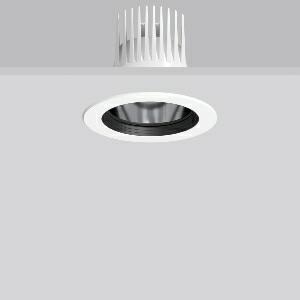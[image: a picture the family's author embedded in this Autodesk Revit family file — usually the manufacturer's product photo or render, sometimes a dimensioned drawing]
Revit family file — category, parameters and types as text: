
# Revit family: heledon_maxi_e_901763_002_1_8824
name_source: partatom
category: Lighting Fixtures
units: mm (PartAtom-declared; Revit-internal decimal feet)

## family parameters
Cut with Voids When Loaded = No
Host = Face
Light Source = No
Part Type = Normal
Room Calculation Point = No
Round Connector Dimension = Use Diameter
Shared = No

## types (1)
- HELEDON maxi E (1 x LED Modul 940, 4400 lm, 4000)
    Apparent Load = 35 VA
    Approval mark = CE
    CIE Flux Codes = 100 100 100 100 100
    Color Rendering = 92
    Color Temperature = 4000
    Default Elevation = 1800 mm
    Description = Series: HELEDON maxi
Round recessed downlight. Housing: die-cast aluminium, powder-coated. Black plastic ring and recessed LED to prevent glare from the side. Optical assembly with reflector made of MIRO-Silver with 98% total light reflection for outstanding efficiency - can be changed without tools. Best colour rendering index Ra>90. Suitable for Recessed ceiling mounting. Installation without tools thanks to spring fastening system. Including separate LED converter with connecting cable 600 mm.High quality converter without flickering and stroboscopic effect. Through-wiring box (5 pole) available as accessory. The following accessories can be mounted without use of tools: interchangeable lenses, decorative glasses, honeycomb louvre, clear and frosted diffusers, white interchangeable plastic ring. 
Colour: traffic white, matt (RAL 9016)
Diameter: 162 mm
Height: 3 mm
Cut-out diameter: 152 mm
Recess height: 200 mm
Luminaire: recess height: 135 mm
Lamp: LED
Socket: without socket
Colour temperature: 4000K
Colour rendering index (CRI): 92
System power: 35 W
Rated luminous flux: 4400 lm
Luminous efficiency: 126 lm/W
Control gear: Regulated power supply
Protection class: II
Type of protection: IP 20
    Height = 0 mm  [stored 0 ft]
    Lamp = 1 x LED Modul 940
    Lamp Light Flux = 4400 lm
    Lamp count = 1
    Length = 162 mm
    Lifetime = 50000 h
    Luminous efficacy = 126 lm/W
    Manufacturer = RZB
    ModVariant = No
    Model = 901763.002.1
    Mounting Place = Ceiling
    Mounting Type = Recessed
    Number of Poles = 1
    OnlyDefault = Yes
    Power Factor = 1
    Product Name = HELEDON maxi E
    Product group = Recessed downlights
    ProductGroupID = 402
    Protection Class = Protection class II
    Protection Degree = IP 20
    RLX_Detail_Level = 1
    RLX_Emergency_Light_Flux = 0 lm
    RLX_Emergency_Type = 0
    RLX_Emergency_Type_DB = No
    RlxData = <blob elided: 119245 chars, md5=5bbfcdbf>
    Socket = socket
    Standby Power = 0 W
    System Light Flux = 4400 lm
    System Power = 35 W
    Type Comments = Product without accessories
    Type Image = 901662.002.jpg
    URL = http://relux.com
    VarID = ---
    Voltage = 230 V
    Voltage Range = 220-240 V
    Weight = 0.00 kg
    Width = 0 mm  [stored 0 ft]

note: [stored X ft] marks values corroborated as IEEE doubles in the binary element streams (Revit-internal decimal feet)

## geometry (parser evidence)
native form markers: Blend x4, Sweep x12
no freeform markers — native parametric forms only
